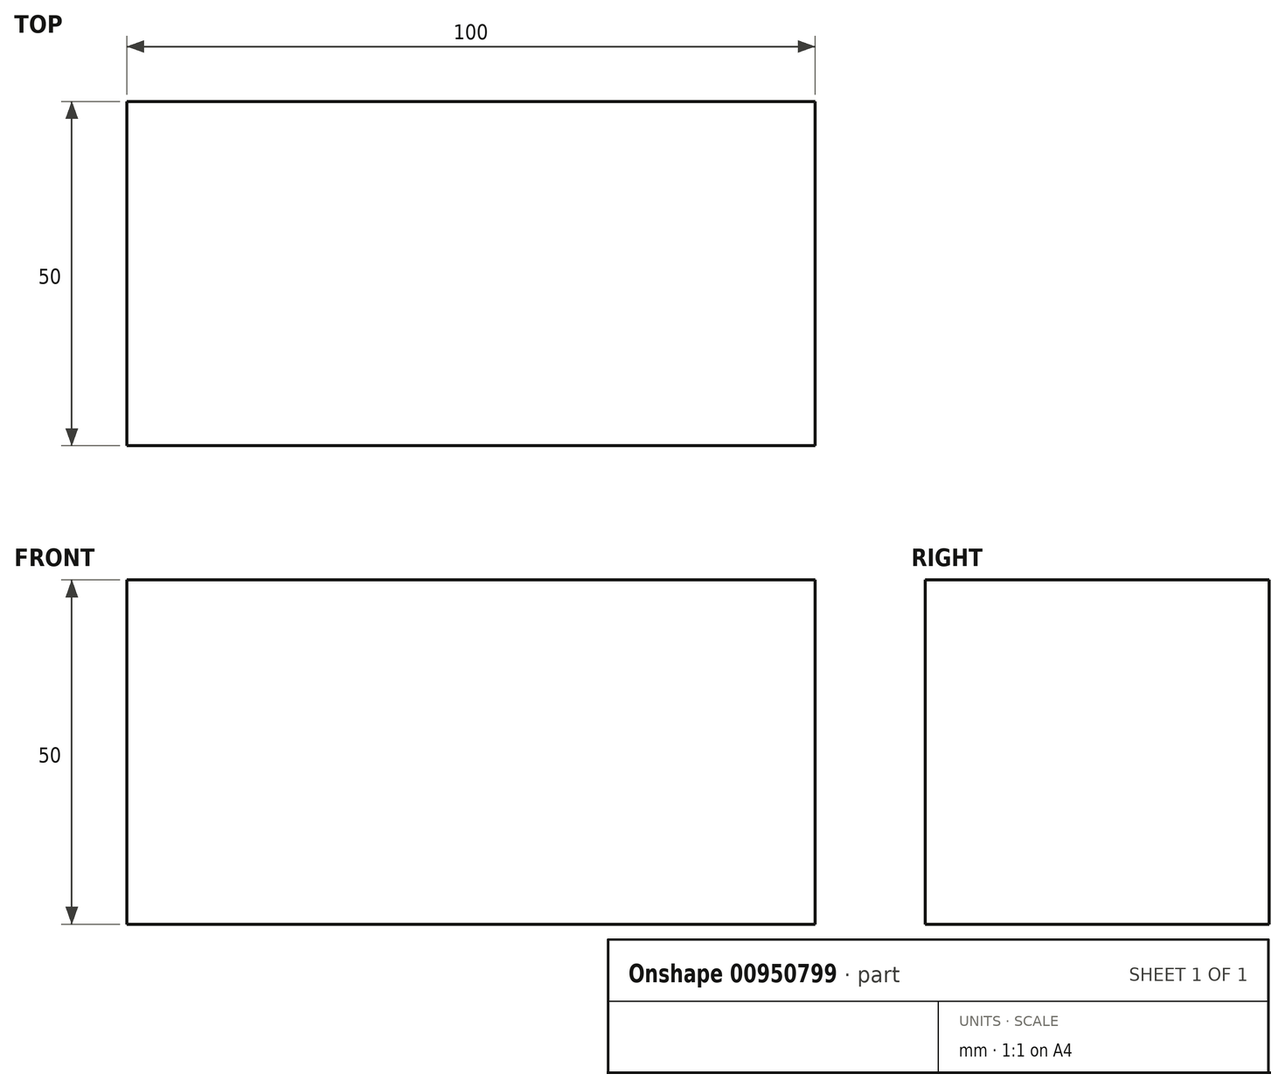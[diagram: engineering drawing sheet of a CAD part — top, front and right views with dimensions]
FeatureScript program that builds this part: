
annotation { "Feature Type Name" : "Feature", "Feature Type Description" : "" }
export const myFeature = defineFeature(function(context is Context, id is Id, definition is map)
    precondition{}
    {
        {
            var Q0;
            Q0=qCreatedBy(makeId("Front.planeOp"),FACE);
            var sketch = newSketch(context, id + "F0", { "sketchPlane" : qUnion([Q0])});
            skLineSegment(sketch, "E0.bottom", {"start": v(-36.63, 111.61) * mm, "end": v(63.37, 111.61) * mm});
            skLineSegment(sketch, "E0.top", {"start": v(-36.63, 61.61) * mm, "end": v(63.37, 61.61) * mm});
            skLineSegment(sketch, "E0.left", {"start": v(-36.63, 111.61) * mm, "end": v(-36.63, 61.61) * mm});
            skLineSegment(sketch, "E0.right", {"start": v(63.37, 111.61) * mm, "end": v(63.37, 61.61) * mm});
            skSolve(sketch);
        }
        {
            var Q0;
            Q0 = qSketchRegion(id + "F0", true);
            extrude(context, id + "F1", {"entities" : qUnion([Q0]), "depth" : 50 * mm, "offsetDistance" : 25 * mm});
        }
    });
